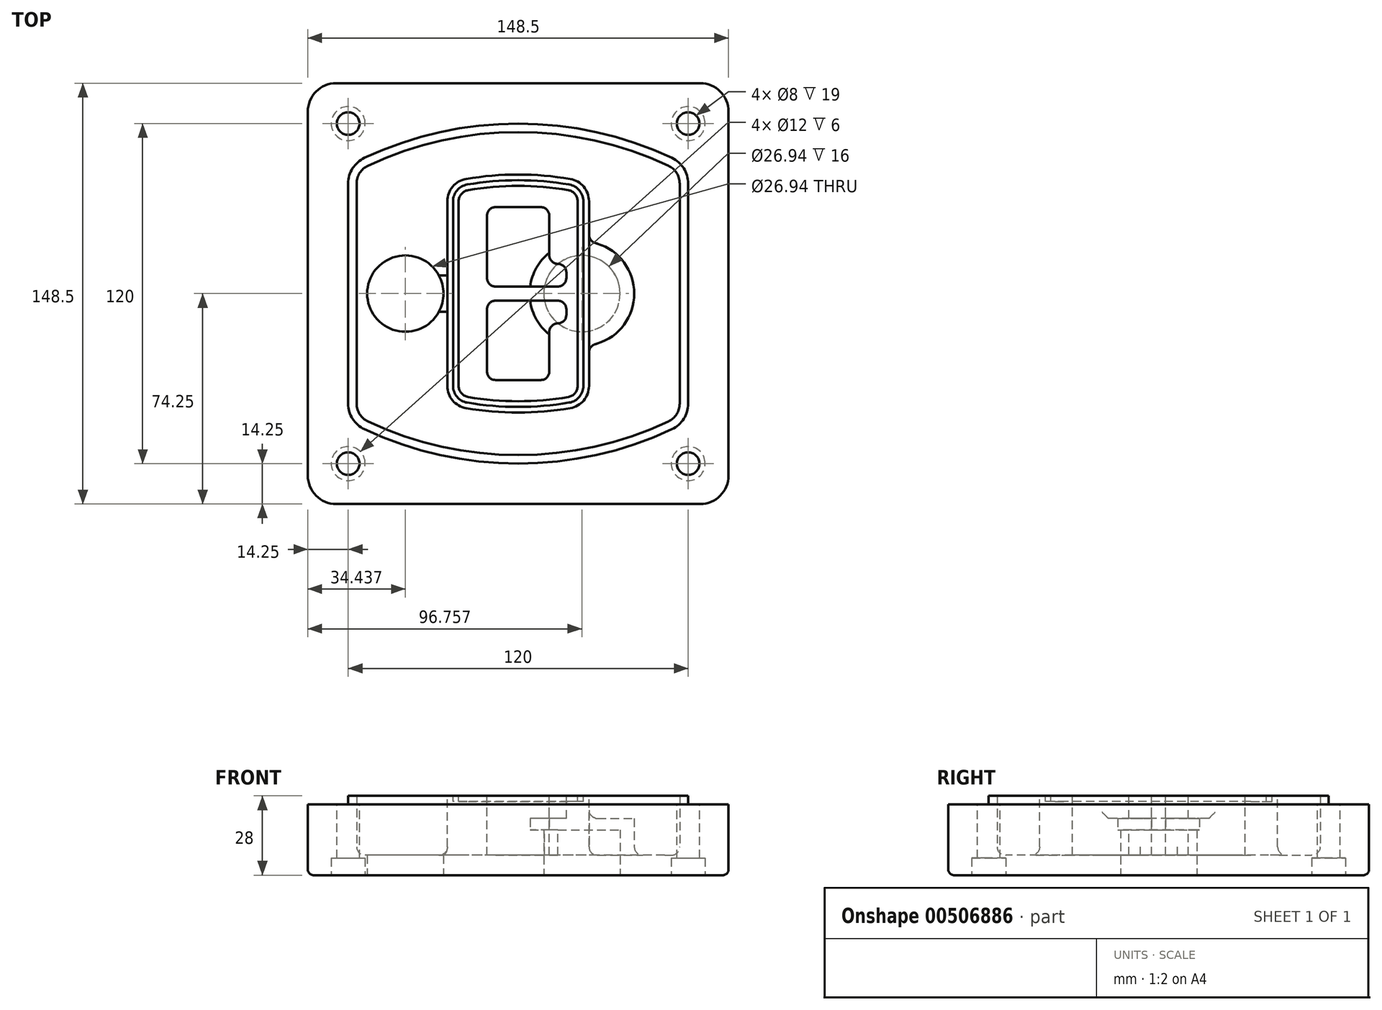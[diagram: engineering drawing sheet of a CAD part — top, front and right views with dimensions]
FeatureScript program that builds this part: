
annotation { "Feature Type Name" : "Feature", "Feature Type Description" : "" }
export const myFeature = defineFeature(function(context is Context, id is Id, definition is map)
    precondition{}
    {
        {
            var Q0;
            Q0=qCreatedBy(makeId("Top.planeOp"),FACE);
            var sketch = newSketch(context, id + "F0", { "sketchPlane" : qUnion([Q0])});
            skPoint(sketch, "E0.rect.middle", {"position": v(0, 0) * mm});
            skLineSegment(sketch, "E1.bottom", {"start": v(-64.25, -74.25) * mm, "end": v(64.25, -74.25) * mm});
            skLineSegment(sketch, "E1.top", {"start": v(-64.25, 74.25) * mm, "end": v(64.25, 74.25) * mm});
            skLineSegment(sketch, "E1.left", {"start": v(-74.25, -64.25) * mm, "end": v(-74.25, 64.25) * mm});
            skLineSegment(sketch, "E1.right", {"start": v(74.25, -64.25) * mm, "end": v(74.25, 64.25) * mm});
            skLineSegment(sketch, "E2", {"start": v(-74.25, 74.25) * mm, "end": v(74.25, -74.25) * mm, "construction": true});
            skLineSegment(sketch, "E3", {"start": v(74.25, 74.25) * mm, "end": v(-74.25, -74.25) * mm, "construction": true});
            skCircle(sketch, "E4", {"center": v(-60, 60) * mm, "radius": 4 * mm});
            skCircle(sketch, "E5", {"center": v(60, 60) * mm, "radius": 4 * mm});
            skCircle(sketch, "E6", {"center": v(60, -60) * mm, "radius": 4 * mm});
            skCircle(sketch, "E7", {"center": v(-60, -60) * mm, "radius": 4 * mm});
            skLineSegment(sketch, "E8", {"start": v(-60, 60) * mm, "end": v(60, 60) * mm, "construction": true});
            skLineSegment(sketch, "E9", {"start": v(60, 60) * mm, "end": v(60, -60) * mm, "construction": true});
            skLineSegment(sketch, "E10", {"start": v(60, -60) * mm, "end": v(-60, -60) * mm, "construction": true});
            skLineSegment(sketch, "E11", {"start": v(-60, -60) * mm, "end": v(-60, 60) * mm, "construction": true});
            skLineSegment(sketch, "E12", {"start": v(-60, 38.83) * mm, "end": v(-60, -38.83) * mm});
            skLineSegment(sketch, "E13", {"start": v(60, 38.83) * mm, "end": v(60, -38.83) * mm});
            skArc(sketch, "E14", {"start": v(54.26, 47.88) * mm, "mid": v(0, 60) * mm, "end": v(-54.26, 47.88) * mm});
            skArc(sketch, "E15", {"start": v(-54.26, -47.88) * mm, "mid": v(0, -60) * mm, "end": v(54.26, -47.88) * mm});
            skLineSegment(sketch, "E16", {"start": v(-60, 0) * mm, "end": v(60, 0) * mm, "construction": true});
            skPoint(sketch, "E17.visualSharp", {"position": v(-60, -45) * mm});
            skArc(sketch, "E17.filletArc", {"start": v(-60, -38.83) * mm, "mid": v(-58.44, -44.2) * mm, "end": v(-54.26, -47.88) * mm});
            skPoint(sketch, "E18.visualSharp", {"position": v(-60, 45) * mm});
            skArc(sketch, "E18.filletArc", {"start": v(-54.26, 47.88) * mm, "mid": v(-58.44, 44.2) * mm, "end": v(-60, 38.83) * mm});
            skPoint(sketch, "E19.visualSharp", {"position": v(60, 45) * mm});
            skArc(sketch, "E19.filletArc", {"start": v(60, 38.83) * mm, "mid": v(58.44, 44.2) * mm, "end": v(54.26, 47.88) * mm});
            skPoint(sketch, "E20.visualSharp", {"position": v(60, -45) * mm});
            skArc(sketch, "E20.filletArc", {"start": v(54.26, -47.88) * mm, "mid": v(58.44, -44.2) * mm, "end": v(60, -38.83) * mm});
            skPoint(sketch, "E21.visualSharp", {"position": v(-74.25, 74.25) * mm});
            skArc(sketch, "E21.filletArc", {"start": v(-64.25, 74.25) * mm, "mid": v(-71.32, 71.32) * mm, "end": v(-74.25, 64.25) * mm});
            skPoint(sketch, "E22.visualSharp", {"position": v(74.25, 74.25) * mm});
            skArc(sketch, "E22.filletArc", {"start": v(74.25, 64.25) * mm, "mid": v(71.32, 71.32) * mm, "end": v(64.25, 74.25) * mm});
            skPoint(sketch, "E23.visualSharp", {"position": v(74.25, -74.25) * mm});
            skArc(sketch, "E23.filletArc", {"start": v(64.25, -74.25) * mm, "mid": v(71.32, -71.32) * mm, "end": v(74.25, -64.25) * mm});
            skPoint(sketch, "E24.visualSharp", {"position": v(-74.25, -74.25) * mm});
            skArc(sketch, "E24.filletArc", {"start": v(-74.25, -64.25) * mm, "mid": v(-71.32, -71.32) * mm, "end": v(-64.25, -74.25) * mm});
            skArc(sketch, "E25.0", {"start": v(57, 38.83) * mm, "mid": v(55.9, 42.58) * mm, "end": v(52.98, 45.17) * mm});
            skLineSegment(sketch, "E25.1", {"start": v(57, 38.83) * mm, "end": v(57, -38.83) * mm});
            skArc(sketch, "E25.2", {"start": v(52.98, -45.17) * mm, "mid": v(55.9, -42.58) * mm, "end": v(57, -38.83) * mm});
            skArc(sketch, "E25.3", {"start": v(-52.98, -45.17) * mm, "mid": v(0, -57) * mm, "end": v(52.98, -45.17) * mm});
            skArc(sketch, "E25.4", {"start": v(-57, -38.83) * mm, "mid": v(-55.9, -42.58) * mm, "end": v(-52.98, -45.17) * mm});
            skArc(sketch, "E25.5", {"start": v(52.98, 45.17) * mm, "mid": v(0, 57) * mm, "end": v(-52.98, 45.17) * mm});
            skLineSegment(sketch, "E25.6", {"start": v(-57, 38.83) * mm, "end": v(-57, -38.83) * mm});
            skArc(sketch, "E25.7", {"start": v(-52.98, 45.17) * mm, "mid": v(-55.9, 42.58) * mm, "end": v(-57, 38.83) * mm});
            skArc(sketch, "E26.0", {"start": v(-55.96, 51.5) * mm, "mid": v(-61.82, 46.33) * mm, "end": v(-64, 38.83) * mm});
            skArc(sketch, "E26.1", {"start": v(55.96, 51.5) * mm, "mid": v(0, 64) * mm, "end": v(-55.96, 51.5) * mm});
            skArc(sketch, "E26.2", {"start": v(64, 38.83) * mm, "mid": v(61.82, 46.33) * mm, "end": v(55.96, 51.5) * mm});
            skLineSegment(sketch, "E26.3", {"start": v(64, 38.83) * mm, "end": v(64, -38.83) * mm});
            skArc(sketch, "E26.4", {"start": v(55.96, -51.5) * mm, "mid": v(61.82, -46.33) * mm, "end": v(64, -38.83) * mm});
            skLineSegment(sketch, "E26.5", {"start": v(-64, 38.83) * mm, "end": v(-64, -38.83) * mm});
            skArc(sketch, "E26.6", {"start": v(-55.96, -51.5) * mm, "mid": v(0, -64) * mm, "end": v(55.96, -51.5) * mm});
            skArc(sketch, "E26.7", {"start": v(-64, -38.83) * mm, "mid": v(-61.82, -46.33) * mm, "end": v(-55.96, -51.5) * mm});
            skSolve(sketch);
        }
        {
            var Q0;
            Q0=makeQuery(id+"F0.imprint","IMPRINT",FACE,{"disambiguationData":[TD([[makeQuery(id+"F0.imprint","IMPRINT",EDGE,{"derivedFrom":sQuery(id+"F0.wireOp",EDGE,"E1.bottom")}),1.0]])]});
            var Q1;
            Q1=makeQuery(id+"F0.imprint","IMPRINT",FACE,{"disambiguationData":[TD([[makeQuery(id+"F0.imprint","IMPRINT",EDGE,{"derivedFrom":sQuery(id+"F0.wireOp",EDGE,"E12")}),1.0]])]});
            var Q2;
            Q2=makeQuery(id+"F0.imprint","IMPRINT",FACE,{"disambiguationData":[TD([[makeQuery(id+"F0.imprint","IMPRINT",EDGE,{"derivedFrom":sQuery(id+"F0.wireOp",EDGE,"E25.0")}),1.0]])]});
            var Q3;
            Q3=makeQuery(id+"F0.imprint","IMPRINT",FACE,{"disambiguationData":[TD([[makeQuery(id+"F0.imprint","IMPRINT",EDGE,{"derivedFrom":sQuery(id+"F0.wireOp",EDGE,"E12")}),-1.0]])]});
            extrude(context, id + "F1", {"entities" : qUnion([Q0, Q1, Q2, Q3]), "oppositeDirection" : true, "depth" : 25 * mm});
        }
        {
            var Q0;
            Q0=makeQuery(id+"F0.imprint","IMPRINT",FACE,{"disambiguationData":[TD([[makeQuery(id+"F0.imprint","IMPRINT",EDGE,{"derivedFrom":sQuery(id+"F0.wireOp",EDGE,"E12")}),1.0]])]});
            extrude(context, id + "F2", {"entities" : qUnion([Q0]), "operationType" : NewBodyOperationType.ADD, "depth" : 3 * mm});
        }
        {
            var Q0;
            Q0=makeQuery(id+"F0.imprint","IMPRINT",FACE,{"disambiguationData":[TD([[makeQuery(id+"F0.imprint","IMPRINT",EDGE,{"derivedFrom":sQuery(id+"F0.wireOp",EDGE,"E25.0")}),1.0]])]});
            extrude(context, id + "F3", {"entities" : qUnion([Q0]), "operationType" : NewBodyOperationType.REMOVE, "oppositeDirection" : true, "depth" : 18 * mm});
        }
        {
            var Q0;
            Q0=makeQuery(id+"F2.opExtrude","CAP_FACE",FACE,{"disambiguationData":[OSD([sQuery(id+"F0.wireOp",EDGE,"E12"),sQuery(id+"F0.wireOp",EDGE,"E13"),sQuery(id+"F0.wireOp",EDGE,"E14"),sQuery(id+"F0.wireOp",EDGE,"E15"),sQuery(id+"F0.wireOp",EDGE,"E17.filletArc"),sQuery(id+"F0.wireOp",EDGE,"E18.filletArc"),sQuery(id+"F0.wireOp",EDGE,"E19.filletArc"),sQuery(id+"F0.wireOp",EDGE,"E20.filletArc"),sQuery(id+"F0.wireOp",EDGE,"E25.0"),sQuery(id+"F0.wireOp",EDGE,"E25.1"),sQuery(id+"F0.wireOp",EDGE,"E25.2"),sQuery(id+"F0.wireOp",EDGE,"E25.3"),sQuery(id+"F0.wireOp",EDGE,"E25.4"),sQuery(id+"F0.wireOp",EDGE,"E25.5"),sQuery(id+"F0.wireOp",EDGE,"E25.6"),sQuery(id+"F0.wireOp",EDGE,"E25.7")])],"isStart":false});
            var sketch = newSketch(context, id + "F4", { "sketchPlane" : qUnion([Q0])});
            skArc(sketch, "E27.0", {"start": v(-18.34, -40.45) * mm, "mid": v(0, -42) * mm, "end": v(18.34, -40.45) * mm});
            skArc(sketch, "E28.0", {"start": v(18.34, 40.45) * mm, "mid": v(0, 42) * mm, "end": v(-18.34, 40.45) * mm});
            skLineSegment(sketch, "E29", {"start": v(-25, 32.57) * mm, "end": v(-25, -32.57) * mm});
            skLineSegment(sketch, "E30", {"start": v(25, 32.57) * mm, "end": v(25, -32.57) * mm});
            skLineSegment(sketch, "E31", {"start": v(-25, 39.1) * mm, "end": v(25, 39.1) * mm, "construction": true});
            skLineSegment(sketch, "E32", {"start": v(-25, -39.1) * mm, "end": v(25, -39.1) * mm, "construction": true});
            skPoint(sketch, "E33.visualSharp", {"position": v(-25, 39.1) * mm});
            skArc(sketch, "E33.filletArc", {"start": v(-18.34, 40.45) * mm, "mid": v(-23.11, 37.73) * mm, "end": v(-25, 32.57) * mm});
            skPoint(sketch, "E34.visualSharp", {"position": v(25, 39.1) * mm});
            skArc(sketch, "E34.filletArc", {"start": v(25, 32.57) * mm, "mid": v(23.11, 37.73) * mm, "end": v(18.34, 40.45) * mm});
            skPoint(sketch, "E35.visualSharp", {"position": v(25, -39.1) * mm});
            skArc(sketch, "E35.filletArc", {"start": v(18.34, -40.45) * mm, "mid": v(23.11, -37.73) * mm, "end": v(25, -32.57) * mm});
            skPoint(sketch, "E36.visualSharp", {"position": v(-25, -39.1) * mm});
            skArc(sketch, "E36.filletArc", {"start": v(-25, -32.57) * mm, "mid": v(-23.11, -37.73) * mm, "end": v(-18.34, -40.45) * mm});
            skArc(sketch, "E37.0", {"start": v(52.98, 45.17) * mm, "mid": v(0, 57) * mm, "end": v(-52.98, 45.17) * mm});
            skArc(sketch, "E37.1", {"start": v(-52.98, 45.17) * mm, "mid": v(-55.9, 42.58) * mm, "end": v(-57, 38.83) * mm});
            skLineSegment(sketch, "E37.2", {"start": v(-57, 38.83) * mm, "end": v(-57, -38.83) * mm});
            skArc(sketch, "E37.3", {"start": v(-57, -38.83) * mm, "mid": v(-55.9, -42.58) * mm, "end": v(-52.98, -45.17) * mm});
            skArc(sketch, "E37.4", {"start": v(-52.98, -45.17) * mm, "mid": v(0, -57) * mm, "end": v(52.98, -45.17) * mm});
            skArc(sketch, "E37.5", {"start": v(52.98, -45.17) * mm, "mid": v(55.9, -42.58) * mm, "end": v(57, -38.83) * mm});
            skLineSegment(sketch, "E37.6", {"start": v(57, 38.83) * mm, "end": v(57, -38.83) * mm});
            skArc(sketch, "E37.7", {"start": v(57, 38.83) * mm, "mid": v(55.9, 42.58) * mm, "end": v(52.98, 45.17) * mm});
            skLineSegment(sketch, "E38.0", {"start": v(23, 32.57) * mm, "end": v(23, -32.57) * mm});
            skArc(sketch, "E38.1", {"start": v(18, -38.48) * mm, "mid": v(21.58, -36.44) * mm, "end": v(23, -32.57) * mm});
            skArc(sketch, "E38.2", {"start": v(-18, -38.48) * mm, "mid": v(0, -40) * mm, "end": v(18, -38.48) * mm});
            skArc(sketch, "E38.3", {"start": v(-23, -32.57) * mm, "mid": v(-21.58, -36.44) * mm, "end": v(-18, -38.48) * mm});
            skLineSegment(sketch, "E38.4", {"start": v(-23, 32.57) * mm, "end": v(-23, -32.57) * mm});
            skArc(sketch, "E38.5", {"start": v(23, 32.57) * mm, "mid": v(21.58, 36.44) * mm, "end": v(18, 38.48) * mm});
            skArc(sketch, "E38.6", {"start": v(-18, 38.48) * mm, "mid": v(-21.58, 36.44) * mm, "end": v(-23, 32.57) * mm});
            skArc(sketch, "E38.7", {"start": v(18, 38.48) * mm, "mid": v(0, 40) * mm, "end": v(-18, 38.48) * mm});
            skArc(sketch, "E39.0", {"start": v(21, 32.57) * mm, "mid": v(20.06, 35.15) * mm, "end": v(17.67, 36.5) * mm});
            skLineSegment(sketch, "E39.1", {"start": v(21, 32.57) * mm, "end": v(21, -32.57) * mm});
            skArc(sketch, "E39.2", {"start": v(17.67, -36.5) * mm, "mid": v(20.06, -35.15) * mm, "end": v(21, -32.57) * mm});
            skArc(sketch, "E39.3", {"start": v(-17.67, -36.5) * mm, "mid": v(0, -38) * mm, "end": v(17.67, -36.5) * mm});
            skArc(sketch, "E39.4", {"start": v(-21, -32.57) * mm, "mid": v(-20.06, -35.15) * mm, "end": v(-17.67, -36.5) * mm});
            skArc(sketch, "E39.5", {"start": v(17.67, 36.5) * mm, "mid": v(0, 38) * mm, "end": v(-17.67, 36.5) * mm});
            skLineSegment(sketch, "E39.6", {"start": v(-21, 32.57) * mm, "end": v(-21, -32.57) * mm});
            skArc(sketch, "E39.7", {"start": v(-17.67, 36.5) * mm, "mid": v(-20.06, 35.15) * mm, "end": v(-21, 32.57) * mm});
            skLineSegment(sketch, "E40", {"start": v(-25, 0) * mm, "end": v(25, 0) * mm, "construction": true});
            skLineSegment(sketch, "E41", {"start": v(-11, 5.5) * mm, "end": v(-11, 27.5) * mm});
            skLineSegment(sketch, "E42", {"start": v(-8, 30.5) * mm, "end": v(8, 30.5) * mm});
            skLineSegment(sketch, "E43", {"start": v(11, 27.5) * mm, "end": v(11, 13.5) * mm});
            skLineSegment(sketch, "E44", {"start": v(14, 10.5) * mm, "end": v(14, 10.5) * mm});
            skLineSegment(sketch, "E45", {"start": v(17, 7.5) * mm, "end": v(17, 5.5) * mm});
            skLineSegment(sketch, "E46", {"start": v(14, 2.5) * mm, "end": v(-8, 2.5) * mm});
            skPoint(sketch, "E47.visualSharp", {"position": v(-11, 30.5) * mm});
            skArc(sketch, "E47.filletArc", {"start": v(-8, 30.5) * mm, "mid": v(-10.12, 29.62) * mm, "end": v(-11, 27.5) * mm});
            skPoint(sketch, "E48.visualSharp", {"position": v(11, 30.5) * mm});
            skArc(sketch, "E48.filletArc", {"start": v(11, 27.5) * mm, "mid": v(10.12, 29.62) * mm, "end": v(8, 30.5) * mm});
            skPoint(sketch, "E49.visualSharp", {"position": v(11, 10.5) * mm});
            skArc(sketch, "E49.filletArc", {"start": v(11, 13.5) * mm, "mid": v(11.88, 11.38) * mm, "end": v(14, 10.5) * mm});
            skPoint(sketch, "E50.visualSharp", {"position": v(17, 10.5) * mm});
            skArc(sketch, "E50.filletArc", {"start": v(17, 7.5) * mm, "mid": v(16.12, 9.62) * mm, "end": v(14, 10.5) * mm});
            skPoint(sketch, "E51.visualSharp", {"position": v(17, 2.5) * mm});
            skArc(sketch, "E51.filletArc", {"start": v(14, 2.5) * mm, "mid": v(16.12, 3.38) * mm, "end": v(17, 5.5) * mm});
            skPoint(sketch, "E52.visualSharp", {"position": v(-11, 2.5) * mm});
            skArc(sketch, "E52.filletArc", {"start": v(-11, 5.5) * mm, "mid": v(-10.12, 3.38) * mm, "end": v(-8, 2.5) * mm});
            skLineSegment(sketch, "E53.0.MirrorCS", {"start": v(14, -2.5) * mm, "end": v(-8, -2.5) * mm});
            skArc(sketch, "E54.0.MirrorCS", {"start": v(-11, -5.5) * mm, "mid": v(-10.12, -3.38) * mm, "end": v(-8, -2.5) * mm});
            skLineSegment(sketch, "E55.0.MirrorCS", {"start": v(-11, -5.5) * mm, "end": v(-11, -27.5) * mm});
            skArc(sketch, "E56.0.MirrorCS", {"start": v(-8, -30.5) * mm, "mid": v(-10.12, -29.62) * mm, "end": v(-11, -27.5) * mm});
            skLineSegment(sketch, "E57.0.MirrorCS", {"start": v(-8, -30.5) * mm, "end": v(8, -30.5) * mm});
            skArc(sketch, "E58.0.MirrorCS", {"start": v(11, -27.5) * mm, "mid": v(10.12, -29.62) * mm, "end": v(8, -30.5) * mm});
            skLineSegment(sketch, "E59.0.MirrorCS", {"start": v(11, -27.5) * mm, "end": v(11, -13.5) * mm});
            skArc(sketch, "E60.0.MirrorCS", {"start": v(11, -13.5) * mm, "mid": v(11.88, -11.38) * mm, "end": v(14, -10.5) * mm});
            skArc(sketch, "E61.0.MirrorCS", {"start": v(17, -7.5) * mm, "mid": v(16.12, -9.62) * mm, "end": v(14, -10.5) * mm});
            skLineSegment(sketch, "E62.0.MirrorCS", {"start": v(17, -7.5) * mm, "end": v(17, -5.5) * mm});
            skArc(sketch, "E63.0.MirrorCS", {"start": v(14, -2.5) * mm, "mid": v(16.12, -3.38) * mm, "end": v(17, -5.5) * mm});
            skSolve(sketch);
        }
        {
            var Q0;
            Q0=makeQuery(id+"F4.imprint","IMPRINT",FACE,{"disambiguationData":[TD([[makeQuery(id+"F4.imprint","IMPRINT",EDGE,{"derivedFrom":sQuery(id+"F4.wireOp",EDGE,"E27.0")}),1.0]])]});
            var Q1;
            Q1=makeQuery(id+"F4.imprint","IMPRINT",FACE,{"disambiguationData":[TD([[makeQuery(id+"F4.imprint","IMPRINT",EDGE,{"derivedFrom":sQuery(id+"F4.wireOp",EDGE,"E38.0")}),-1.0]])]});
            var Q2;
            Q2=makeQuery(id+"F4.imprint","IMPRINT",FACE,{"disambiguationData":[TD([[makeQuery(id+"F4.imprint","IMPRINT",EDGE,{"derivedFrom":sQuery(id+"F4.wireOp",EDGE,"E39.0")}),1.0]])]});
            extrude(context, id + "F5", {"entities" : qUnion([Q0, Q1, Q2]), "operationType" : NewBodyOperationType.ADD, "endBound" : BoundingType.UP_TO_NEXT, "oppositeDirection" : true, "depth" : 25 * mm});
        }
        {
            var Q0;
            Q0=makeQuery(id+"F4.imprint","IMPRINT",FACE,{"disambiguationData":[TD([[makeQuery(id+"F4.imprint","IMPRINT",EDGE,{"derivedFrom":sQuery(id+"F4.wireOp",EDGE,"E38.0")}),-1.0]])]});
            extrude(context, id + "F6", {"entities" : qUnion([Q0]), "operationType" : NewBodyOperationType.REMOVE, "oppositeDirection" : true, "depth" : 2 * mm});
        }
        {
            var Q0;
            Q0=makeQuery(id+"F1.opExtrude","CAP_FACE",FACE,{"disambiguationData":[OSD([sQuery(id+"F0.wireOp",EDGE,"E1.bottom"),sQuery(id+"F0.wireOp",EDGE,"E1.top"),sQuery(id+"F0.wireOp",EDGE,"E1.left"),sQuery(id+"F0.wireOp",EDGE,"E1.right"),sQuery(id+"F0.wireOp",EDGE,"E4"),sQuery(id+"F0.wireOp",EDGE,"E5"),sQuery(id+"F0.wireOp",EDGE,"E6"),sQuery(id+"F0.wireOp",EDGE,"E7"),sQuery(id+"F0.wireOp",EDGE,"E21.filletArc"),sQuery(id+"F0.wireOp",EDGE,"E22.filletArc"),sQuery(id+"F0.wireOp",EDGE,"E23.filletArc"),sQuery(id+"F0.wireOp",EDGE,"E24.filletArc")])],"isStart":false});
            var sketch = newSketch(context, id + "F7", { "sketchPlane" : qUnion([Q0])});
            skCircle(sketch, "E64", {"center": v(22.5, 0) * mm, "radius": 13.47 * mm});
            skCircle(sketch, "E65", {"center": v(-39.81, 0) * mm, "radius": 13.47 * mm});
            skLineSegment(sketch, "E66", {"start": v(74.25, 0) * mm, "end": v(-74.25, 0) * mm});
            skCircle(sketch, "E67", {"center": v(22.5, 0) * mm, "radius": 18.47 * mm});
            skCircle(sketch, "E68", {"center": v(60, -60) * mm, "radius": 6 * mm});
            skCircle(sketch, "E69", {"center": v(-60, -60) * mm, "radius": 6 * mm});
            skCircle(sketch, "E70", {"center": v(-60, 60) * mm, "radius": 6 * mm});
            skCircle(sketch, "E71", {"center": v(60, 60) * mm, "radius": 6 * mm});
            skSolve(sketch);
        }
        {
            var Q0;
            {var subQ1=sQuery(id+"F7.wireOp",EDGE,"E66");var subQ4=sQuery(id+"F7.wireOp",EDGE,"E64");var subQ6=makeQuery(id+"F7.imprint","INTERSECT",VERTEX,{"disambiguationData":[OD(0.0)],"derivedFrom":[subQ4,subQ1]});Q0=makeQuery(id+"F7.imprint","IMPRINT",FACE,{"disambiguationData":[TD([[makeQuery(id+"F7.imprint","IMPRINT",EDGE,{"disambiguationData":[TD([[subQ6,-1.0]])],"derivedFrom":subQ4}),-1.0]])]});}
            var Q1;
            {var subQ0=sQuery(id+"F7.wireOp",EDGE,"E66");var subQ1=sQuery(id+"F7.wireOp",EDGE,"E64");var subQ3=makeQuery(id+"F7.imprint","INTERSECT",VERTEX,{"disambiguationData":[OD(0.0)],"derivedFrom":[subQ1,subQ0]});Q1=makeQuery(id+"F7.imprint","IMPRINT",FACE,{"disambiguationData":[TD([[makeQuery(id+"F7.imprint","IMPRINT",EDGE,{"disambiguationData":[TD([[subQ3,-1.0]])],"derivedFrom":subQ1}),1.0]])]});}
            var Q2;
            {var subQ0=sQuery(id+"F7.wireOp",EDGE,"E66");var subQ1=sQuery(id+"F7.wireOp",EDGE,"E64");var subQ3=makeQuery(id+"F7.imprint","INTERSECT",VERTEX,{"disambiguationData":[OD(0.0)],"derivedFrom":[subQ1,subQ0]});Q2=makeQuery(id+"F7.imprint","IMPRINT",FACE,{"disambiguationData":[TD([[makeQuery(id+"F7.imprint","IMPRINT",EDGE,{"disambiguationData":[TD([[subQ3,1.0]])],"derivedFrom":subQ1}),1.0]])]});}
            var Q3;
            {var subQ1=sQuery(id+"F7.wireOp",EDGE,"E66");var subQ4=sQuery(id+"F7.wireOp",EDGE,"E64");var subQ6=makeQuery(id+"F7.imprint","INTERSECT",VERTEX,{"disambiguationData":[OD(0.0)],"derivedFrom":[subQ4,subQ1]});Q3=makeQuery(id+"F7.imprint","IMPRINT",FACE,{"disambiguationData":[TD([[makeQuery(id+"F7.imprint","IMPRINT",EDGE,{"disambiguationData":[TD([[subQ6,1.0]])],"derivedFrom":subQ4}),-1.0]])]});}
            extrude(context, id + "F8", {"entities" : qUnion([Q0, Q1, Q2, Q3]), "operationType" : NewBodyOperationType.ADD, "oppositeDirection" : true, "depth" : 20 * mm});
        }
        {
            var Q0;
            {var subQ0=sQuery(id+"F7.wireOp",EDGE,"E66");var subQ1=sQuery(id+"F7.wireOp",EDGE,"E64");var subQ3=makeQuery(id+"F7.imprint","INTERSECT",VERTEX,{"disambiguationData":[OD(0.0)],"derivedFrom":[subQ1,subQ0]});Q0=makeQuery(id+"F7.imprint","IMPRINT",FACE,{"disambiguationData":[TD([[makeQuery(id+"F7.imprint","IMPRINT",EDGE,{"disambiguationData":[TD([[subQ3,-1.0]])],"derivedFrom":subQ1}),1.0]])]});}
            var Q1;
            {var subQ0=sQuery(id+"F7.wireOp",EDGE,"E66");var subQ1=sQuery(id+"F7.wireOp",EDGE,"E64");var subQ3=makeQuery(id+"F7.imprint","INTERSECT",VERTEX,{"disambiguationData":[OD(0.0)],"derivedFrom":[subQ1,subQ0]});Q1=makeQuery(id+"F7.imprint","IMPRINT",FACE,{"disambiguationData":[TD([[makeQuery(id+"F7.imprint","IMPRINT",EDGE,{"disambiguationData":[TD([[subQ3,1.0]])],"derivedFrom":subQ1}),1.0]])]});}
            extrude(context, id + "F9", {"entities" : qUnion([Q0, Q1]), "operationType" : NewBodyOperationType.REMOVE, "oppositeDirection" : true, "depth" : 16 * mm});
        }
        {
            var Q0;
            {var subQ0=sQuery(id+"F7.wireOp",EDGE,"E66");var subQ1=sQuery(id+"F7.wireOp",EDGE,"E65");var subQ3=makeQuery(id+"F7.imprint","INTERSECT",VERTEX,{"disambiguationData":[OD(0.0)],"derivedFrom":[subQ1,subQ0]});Q0=makeQuery(id+"F7.imprint","IMPRINT",FACE,{"disambiguationData":[TD([[makeQuery(id+"F7.imprint","IMPRINT",EDGE,{"disambiguationData":[TD([[subQ3,-1.0]])],"derivedFrom":subQ1}),1.0]])]});}
            var Q1;
            {var subQ0=sQuery(id+"F7.wireOp",EDGE,"E66");var subQ1=sQuery(id+"F7.wireOp",EDGE,"E65");var subQ3=makeQuery(id+"F7.imprint","INTERSECT",VERTEX,{"disambiguationData":[OD(0.0)],"derivedFrom":[subQ1,subQ0]});Q1=makeQuery(id+"F7.imprint","IMPRINT",FACE,{"disambiguationData":[TD([[makeQuery(id+"F7.imprint","IMPRINT",EDGE,{"disambiguationData":[TD([[subQ3,1.0]])],"derivedFrom":subQ1}),1.0]])]});}
            var Q2;
            Q2 = qSketchRegion(id + "F16", true);
            extrude(context, id + "F10", {"entities" : qUnion([Q0, Q1, Q2]), "operationType" : NewBodyOperationType.REMOVE, "oppositeDirection" : true, "depth" : 25 * mm});
        }
        {
            var Q0;
            Q0=makeQuery(id+"F7.imprint","IMPRINT",FACE,{"disambiguationData":[TD([[makeQuery(id+"F7.imprint","IMPRINT",EDGE,{"derivedFrom":sQuery(id+"F7.wireOp",EDGE,"E68")}),1.0]])]});
            var Q1;
            Q1=makeQuery(id+"F7.imprint","IMPRINT",FACE,{"disambiguationData":[TD([[makeQuery(id+"F7.imprint","IMPRINT",EDGE,{"derivedFrom":makeQuery(id+"F1.opExtrude","CAP_EDGE",EDGE,{"disambiguationData":[OSD([sQuery(id+"F0.wireOp",EDGE,"E5")])],"isStart":false})}),-1.0]])]});
            var Q2;
            Q2=makeQuery(id+"F7.imprint","IMPRINT",FACE,{"disambiguationData":[TD([[makeQuery(id+"F7.imprint","IMPRINT",EDGE,{"derivedFrom":sQuery(id+"F7.wireOp",EDGE,"E69")}),1.0]])]});
            var Q3;
            Q3=makeQuery(id+"F7.imprint","IMPRINT",FACE,{"disambiguationData":[TD([[makeQuery(id+"F7.imprint","IMPRINT",EDGE,{"derivedFrom":makeQuery(id+"F1.opExtrude","CAP_EDGE",EDGE,{"disambiguationData":[OSD([sQuery(id+"F0.wireOp",EDGE,"E4")])],"isStart":false})}),-1.0]])]});
            var Q4;
            Q4=makeQuery(id+"F7.imprint","IMPRINT",FACE,{"disambiguationData":[TD([[makeQuery(id+"F7.imprint","IMPRINT",EDGE,{"derivedFrom":sQuery(id+"F7.wireOp",EDGE,"E70")}),1.0]])]});
            var Q5;
            Q5=makeQuery(id+"F7.imprint","IMPRINT",FACE,{"disambiguationData":[TD([[makeQuery(id+"F7.imprint","IMPRINT",EDGE,{"derivedFrom":makeQuery(id+"F1.opExtrude","CAP_EDGE",EDGE,{"disambiguationData":[OSD([sQuery(id+"F0.wireOp",EDGE,"E7")])],"isStart":false})}),-1.0]])]});
            var Q6;
            Q6=makeQuery(id+"F7.imprint","IMPRINT",FACE,{"disambiguationData":[TD([[makeQuery(id+"F7.imprint","IMPRINT",EDGE,{"derivedFrom":sQuery(id+"F7.wireOp",EDGE,"E71")}),1.0]])]});
            var Q7;
            Q7=makeQuery(id+"F7.imprint","IMPRINT",FACE,{"disambiguationData":[TD([[makeQuery(id+"F7.imprint","IMPRINT",EDGE,{"derivedFrom":makeQuery(id+"F1.opExtrude","CAP_EDGE",EDGE,{"disambiguationData":[OSD([sQuery(id+"F0.wireOp",EDGE,"E6")])],"isStart":false})}),-1.0]])]});
            extrude(context, id + "F11", {"entities" : qUnion([Q0, Q1, Q2, Q3, Q4, Q5, Q6, Q7]), "operationType" : NewBodyOperationType.REMOVE, "oppositeDirection" : true, "depth" : 6 * mm});
        }
        {
            var Q0;
            Q0=makeQuery(id+"F9.boolean.opBoolean","COPY",FACE,{"derivedFrom":makeQuery(id+"F9.opExtrude","CAP_FACE",FACE,{"disambiguationData":[OSD([sQuery(id+"F7.wireOp",EDGE,"E64")])],"isStart":false})});
            var sketch = newSketch(context, id + "F12", { "sketchPlane" : qUnion([Q0])});
            skArc(sketch, "E72.0", {"start": v(11, 14.45) * mm, "mid": v(6.45, 9.13) * mm, "end": v(4.2, 2.5) * mm});
            skArc(sketch, "E72.1", {"start": v(4.2, -2.5) * mm, "mid": v(6.45, -9.13) * mm, "end": v(11, -14.45) * mm});
            skLineSegment(sketch, "E73", {"start": v(4.2, -2.5) * mm, "end": v(14, -2.5) * mm});
            skLineSegment(sketch, "E74.0", {"start": v(14, 2.5) * mm, "end": v(4.2, 2.5) * mm});
            skArc(sketch, "E74.1", {"start": v(14, 2.5) * mm, "mid": v(16.12, 3.38) * mm, "end": v(17, 5.5) * mm});
            skLineSegment(sketch, "E74.2", {"start": v(17, 7.5) * mm, "end": v(17, 5.5) * mm});
            skArc(sketch, "E74.3", {"start": v(17, 7.5) * mm, "mid": v(16.12, 9.62) * mm, "end": v(14, 10.5) * mm});
            skArc(sketch, "E74.4", {"start": v(11, 13.5) * mm, "mid": v(11.88, 11.38) * mm, "end": v(14, 10.5) * mm});
            skLineSegment(sketch, "E74.5", {"start": v(11, 14.45) * mm, "end": v(11, 13.5) * mm});
            skLineSegment(sketch, "E74.7", {"start": v(14, -2.5) * mm, "end": v(4.2, -2.5) * mm});
            skArc(sketch, "E74.8", {"start": v(14, -2.5) * mm, "mid": v(16.12, -3.38) * mm, "end": v(17, -5.5) * mm});
            skLineSegment(sketch, "E74.9", {"start": v(17, -7.5) * mm, "end": v(17, -5.5) * mm});
            skArc(sketch, "E74.10", {"start": v(17, -7.5) * mm, "mid": v(16.12, -9.62) * mm, "end": v(14, -10.5) * mm});
            skArc(sketch, "E74.11", {"start": v(11, -13.5) * mm, "mid": v(11.88, -11.38) * mm, "end": v(14, -10.5) * mm});
            skLineSegment(sketch, "E74.12", {"start": v(11, -14.45) * mm, "end": v(11, -13.5) * mm});
            skPoint(sketch, "E75.orphan", {"position": v(11, -27.5) * mm});
            skPoint(sketch, "E76.orphan", {"position": v(-8, -2.5) * mm});
            skPoint(sketch, "E77.orphan", {"position": v(-8, 2.5) * mm});
            skPoint(sketch, "E78.orphan", {"position": v(11, 27.5) * mm});
            skSolve(sketch);
        }
        {
            var Q0;
            {var subQ7=sQuery(id+"F12.wireOp",EDGE,"E72.0");var subQ14=sQuery(id+"F12.wireOp",EDGE,"E72.1");var subQ16=sQuery(id+"F12.wireOp",EDGE,"E74.1");var subQ18=sQuery(id+"F12.wireOp",EDGE,"E74.8");Q0=qUnion([makeQuery(id+"F12.imprint","IMPRINT",FACE,{"disambiguationData":[TD([[makeQuery(id+"F12.imprint","IMPRINT",EDGE,{"derivedFrom":subQ7}),1.0]])]}),makeQuery(id+"F12.imprint","IMPRINT",FACE,{"disambiguationData":[TD([[makeQuery(id+"F12.imprint","IMPRINT",EDGE,{"derivedFrom":subQ14}),1.0]])]}),makeQuery(id+"F12.imprint","IMPRINT",FACE,{"disambiguationData":[TD([[makeQuery(id+"F12.imprint","IMPRINT",EDGE,{"derivedFrom":subQ16}),1.0]])]}),makeQuery(id+"F12.imprint","IMPRINT",FACE,{"disambiguationData":[TD([[makeQuery(id+"F12.imprint","IMPRINT",EDGE,{"derivedFrom":subQ18}),-1.0]])]})]);}
            var Q1;
            Q1=makeQuery(id+"F5.boolean.opBoolean","SPLIT",FACE,{"disambiguationData":[TD([makeQuery(id+"F5.opExtrude","SWEPT_FACE",FACE,{"disambiguationData":[OSD([sQuery(id+"F4.wireOp",EDGE,"E41")])]})])],"derivedFrom":makeQuery(id+"F3.boolean.opBoolean","COPY",FACE,{"derivedFrom":makeQuery(id+"F3.opExtrude","CAP_FACE",FACE,{"disambiguationData":[OSD([sQuery(id+"F0.wireOp",EDGE,"E25.0"),sQuery(id+"F0.wireOp",EDGE,"E25.1"),sQuery(id+"F0.wireOp",EDGE,"E25.2"),sQuery(id+"F0.wireOp",EDGE,"E25.3"),sQuery(id+"F0.wireOp",EDGE,"E25.4"),sQuery(id+"F0.wireOp",EDGE,"E25.5"),sQuery(id+"F0.wireOp",EDGE,"E25.6"),sQuery(id+"F0.wireOp",EDGE,"E25.7")])],"isStart":false})})});
            extrude(context, id + "F13", {"entities" : qUnion([Q0]), "operationType" : NewBodyOperationType.REMOVE, "endBound" : BoundingType.UP_TO_SURFACE, "endBoundEntityFace" : qUnion([Q1]), "depth" : 25 * mm});
        }
        {
            var Q0;
            Q0=makeQuery(id+"F3.boolean.opBoolean","COPY",EDGE,{"derivedFrom":makeQuery(id+"F3.opExtrude","CAP_EDGE",EDGE,{"disambiguationData":[OSD([sQuery(id+"F0.wireOp",EDGE,"E25.6")])],"isStart":false})});
            var Q1;
            Q1=makeQuery(id+"F8.boolean.opBoolean","INTERSECT",EDGE,{"derivedFrom":[makeQuery(id+"F5.opExtrude","SWEPT_FACE",FACE,{"disambiguationData":[OSD([sQuery(id+"F4.wireOp",EDGE,"E30")])]}),makeQuery(id+"F8.opExtrude","CAP_FACE",FACE,{"disambiguationData":[OSD([sQuery(id+"F7.wireOp",EDGE,"E67")])],"isStart":false})]});
            var Q2;
            Q2=makeQuery(id+"F8.boolean.opBoolean","INTERSECT",EDGE,{"disambiguationData":[OD(1.0)],"derivedFrom":[makeQuery(id+"F5.opExtrude","SWEPT_FACE",FACE,{"disambiguationData":[OSD([sQuery(id+"F4.wireOp",EDGE,"E30")])]}),makeQuery(id+"F8.opExtrude","SWEPT_FACE",FACE,{"disambiguationData":[OSD([sQuery(id+"F7.wireOp",EDGE,"E67")])]})]});
            var Q3;
            {var subQ0=sQuery(id+"F4.wireOp",EDGE,"E30");Q3=makeQuery(id+"F8.boolean.opBoolean","SPLIT",EDGE,{"disambiguationData":[TD([makeQuery(id+"F5.opExtrude","SWEPT_FACE",FACE,{"disambiguationData":[OSD([sQuery(id+"F4.wireOp",EDGE,"E35.filletArc")])]})])],"derivedFrom":makeQuery(id+"F5.opExtrude","CAP_EDGE",EDGE,{"disambiguationData":[OSD([subQ0])],"isStart":false})});}
            var Q4;
            {var subQ0=sQuery(id+"F0.wireOp",EDGE,"E25.7");var subQ1=sQuery(id+"F0.wireOp",EDGE,"E25.1");var subQ2=sQuery(id+"F0.wireOp",EDGE,"E25.6");var subQ3=sQuery(id+"F0.wireOp",EDGE,"E25.5");var subQ4=sQuery(id+"F0.wireOp",EDGE,"E25.4");var subQ5=sQuery(id+"F0.wireOp",EDGE,"E25.0");var subQ6=sQuery(id+"F0.wireOp",EDGE,"E25.2");var subQ7=sQuery(id+"F0.wireOp",EDGE,"E25.3");Q4=makeQuery(id+"F8.boolean.opBoolean","INTERSECT",EDGE,{"derivedFrom":[makeQuery(id+"F5.boolean.opBoolean","SPLIT",FACE,{"disambiguationData":[TD([makeQuery(id+"F2.opExtrude","SWEPT_FACE",FACE,{"disambiguationData":[OSD([subQ5])]})])],"derivedFrom":makeQuery(id+"F3.boolean.opBoolean","COPY",FACE,{"derivedFrom":makeQuery(id+"F3.opExtrude","CAP_FACE",FACE,{"disambiguationData":[OSD([subQ5,subQ1,subQ6,subQ7,subQ4,subQ3,subQ2,subQ0])],"isStart":false})})}),makeQuery(id+"F8.opExtrude","SWEPT_FACE",FACE,{"disambiguationData":[OSD([sQuery(id+"F7.wireOp",EDGE,"E67")])]})]});}
            var Q5;
            Q5=makeQuery(id+"F8.boolean.opBoolean","INTERSECT",EDGE,{"disambiguationData":[OD(0.0)],"derivedFrom":[makeQuery(id+"F5.opExtrude","SWEPT_FACE",FACE,{"disambiguationData":[OSD([sQuery(id+"F4.wireOp",EDGE,"E30")])]}),makeQuery(id+"F8.opExtrude","SWEPT_FACE",FACE,{"disambiguationData":[OSD([sQuery(id+"F7.wireOp",EDGE,"E67")])]})]});
            fillet(context, id + "F14", {"entities" : qUnion([Q0, Q1, Q2, Q3, Q4, Q5]), "radius" : 3 * mm, "tangentPropagation" : true, "allowEdgeOverflow" : false});
        }
        {
            var Q0;
            Q0=makeQuery(id+"F1.opExtrude","CAP_EDGE",EDGE,{"disambiguationData":[OSD([sQuery(id+"F0.wireOp",EDGE,"E1.bottom")])],"isStart":false});
            fillet(context, id + "F15", {"entities" : qUnion([Q0]), "radius" : 2 * mm, "tangentPropagation" : true, "allowEdgeOverflow" : false});
        }
    });
